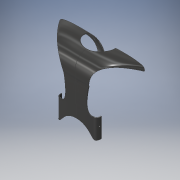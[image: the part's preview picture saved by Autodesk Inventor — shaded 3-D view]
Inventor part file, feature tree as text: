
AUTODESK INVENTOR PART (.ipt)
format: ipt  version: 2019 (Build 230136000, 136)  size: 1,369,600 bytes
history: native  units: mm
features: plane x26, sketch x17, fillet x6, mirror x5, loft x4, extrude x4, chamfer x3, other x1
ambient origin geometry x8: Origin, YZ Plane, XZ Plane, XY Plane, X Axis, Y Axis, Z Axis, Center Point
bodies: Body1 (feature_tree)
feature tree (66):
  sketch  "Sketch1"  dims[d2=55.0mm d5=-107.0mm d13=5.0mm d14=50.0mm]
  plane  "Work Plane1"
  sketch  "Sketch2"  dims[d15=70.0mm d16=5.0mm]
  sketch  "Sketch3"  dims[d17=0.0mm d18=90.0deg d19=0.0mm d20=90.0deg d21=0.0mm d22=90.0deg d23=2.0mm]
  plane  "Work Plane2"
  loft  "Loft2"
  mirror  "Mirror2"
  fillet  "Fillet1"  Radius=5.0mm
  fillet  "Fillet4"  Radius=50.0mm
  plane  "Work Plane3"
  plane  "Work Plane4"
  extrude  "Extrusion1"  Depth=5.0mm
  plane  "Work Plane5"
  extrude  "Extrusion2"  TaperAngle=0.0deg  [1 undecoded]
  fillet  "Fillet5"  [1 undecoded]
  mirror  "Mirror3"
  plane  "Work Plane22"
  plane  "Work Plane6"
  plane  "Work Plane7"
  fillet  "Fillet11"  Radius=2.0mm
  extrude  "Extrusion7"  Depth=87.5mm
  mirror  "Mirror4"
  plane  "Work Plane8"
  plane  "Work Plane9"
  sketch  "Sketch20"  dims[d42=2.0mm]
  plane  "Work Plane10"
  sketch  "Sketch21"  dims[d43=2.0mm]
  plane  "Work Plane11"
  sketch  "Sketch22"  dims[d44=2.0mm]
  loft  "Loft5"
  plane  "Work Plane13"
  sketch  "Sketch25"  dims[d45=2.0mm]
  plane  "Work Plane18"
  loft  "Loft6"
  mirror  "Mirror5"
  plane  "Work Plane19"
  extrude  "Extrusion9"  Depth=2.0mm
  fillet  "Fillet12"  Radius=2.0mm
  fillet  "Fillet14"  Radius=2.0mm
  plane  "Work Plane20"
  plane  "Work Plane21"
  plane  "Work Plane23"
  plane  "Work Plane24"
  plane  "Work Plane25"
  sketch  "Sketch33"  dims[d48=2.0mm]
  plane  "Work Plane26"
  sketch  "Sketch34"  dims[d49=2.0mm d50=2.0mm d51=1.0mm]
  plane  "Work Plane27"
  sketch  "Sketch35"  dims[d79=-25.0mm]
  plane  "Work Plane30"
  sketch  "Sketch38"  dims[d84=2.0mm d85=13.5mm d86=2.5mm d87=5.0mm d88=6.25mm d89=28.0mm d90=0.0mm d91=22.0mm d101=200.0mm d104=5.0mm d105=50.0mm d106=-80.0mm d107=45.0mm d108=3.0mm d109=70.0mm d110=80.0mm d111=3.0mm d112=20.0mm d123=0.0mm d124=90.0deg d125=0.0mm d126=90.0deg d127=0.0mm d128=90.0deg d129=-20.0mm d131=2.0mm d132=80.0mm d133=10.0mm d134=0.0mm d135=0.0mm d136=90.0deg d137=0.0mm d138=90.0deg d139=0.0mm d140=90.0deg d141=3.0mm d142=7.0mm d143=10.0mm d144=0.0mm d145=70.0mm d147=10.0mm d171=35.75mm d174=-8.25mm d177=20.0mm d179=30.0mm d180=5.0mm d181=41.5mm d182=15.0mm d183=10.0mm d184=5.0mm d200=-2.0mm d219=15.0mm d241=2.0mm d242=2.0mm d243=45.0deg d244=1.0mm d245=2.0mm d246=45.0deg d247=0.5mm d248=2.0mm d249=45.0deg d250=5.0mm d251=0.0mm d252=90.0deg d253=0.0mm d254=90.0deg d255=0.0mm d256=90.0deg]
  plane  "Work Plane31"
  plane  "Work Plane35"
  chamfer  "Chamfer7"  Distance=2.0mm
  chamfer  "Chamfer8"  Distance=13.5mm
  chamfer  "Chamfer9"  Distance=2.5mm
  loft  "Loft10"
  mirror  "Mirror9"
  plane  "Work Plane37"
  sketch  "Sketch4"  dims[d29=1.0mm d30=-4.5mm d31=87.5mm]
  sketch  "Sketch5"  dims[d32=0.0mm d33=0.0mm d34=-28.0mm]
  sketch  "Sketch6"  dims[d35=15.0mm d36=3.0mm]
  sketch  "Sketch17"  dims[d37=0.0mm d38=0.0mm d39=2.0mm d40=2.0mm d41=2.0mm]
  sketch  "Sketch27"  dims[d46=2.0mm]
  other  "Edges1"
  sketch  "Sketch28"  dims[d47=2.0mm]
note: 2 required parameter values undecoded (feature->parameter linkage not recoverable at this tier; creation-order binding heuristic only, values carry confidence <= 0.55)
